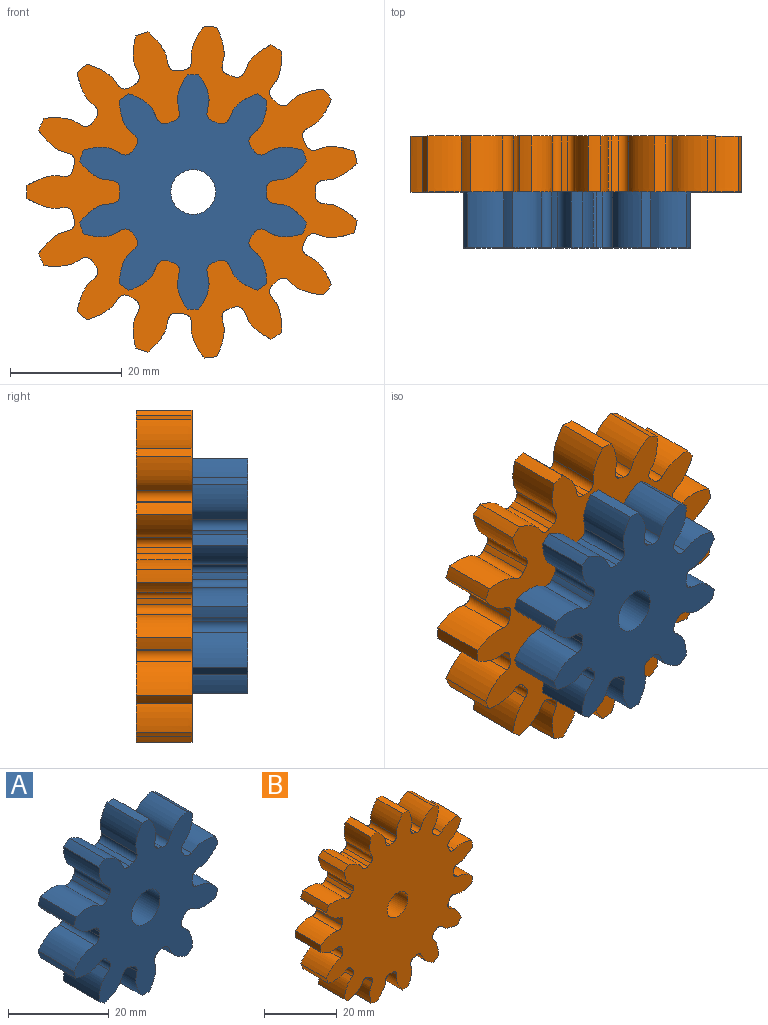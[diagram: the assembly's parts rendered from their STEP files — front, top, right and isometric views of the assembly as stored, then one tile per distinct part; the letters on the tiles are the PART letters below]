
ASSEMBLY  parts=2 mates=1
PART A: 63 faces, bbox 40.6x10x42.1 mm
  f0: cylinder r=21mm len=10mm, axis (0,1,0), area 20.5mm2, adj f9,f12,f53,f60
  f1: cylinder r=21mm len=10mm, axis (0,1,0), area 20.5mm2, adj f9,f12,f13,f55
  f2: cylinder r=21mm len=10mm, axis (0,1,0), area 20.5mm2, adj f9,f12,f43,f50
  f3: cylinder r=21mm len=10mm, axis (0,1,0), area 20.5mm2, adj f9,f12,f45,f58
  f4: cylinder r=21mm len=10mm, axis (0,1,0), area 20.5mm2, adj f9,f12,f33,f40
  f5: cylinder r=21mm len=10mm, axis (0,1,0), area 20.5mm2, adj f9,f12,f28,f35
  f6: cylinder r=21mm len=10mm, axis (0,1,0), area 20.5mm2, adj f9,f12,f23,f30
  f7: cylinder r=21mm len=10mm, axis (0,1,0), area 20.5mm2, adj f9,f12,f25,f48
  f8: cylinder r=21mm len=10mm, axis (0,1,0), area 20.5mm2, adj f9,f12,f20,f38
  f9: plane 42.07x40.62mm, normal (0,-1,0), area 870mm2, adj f0,f1,f2,f3,f4,f5,f6,f7
  f10: cylinder r=4mm len=10mm, axis (0,1,0), area 251.3mm2, adj f9,f12
  f11: cylinder r=21mm len=10mm, axis (0,1,0), area 20.5mm2, adj f9,f12,f15,f18
  f12: plane 42.07x40.62mm, normal (0,1,0), area 870mm2, adj f0,f1,f2,f3,f4,f5,f6,f7
  f13: extruded ~10x5.91mm, area 71mm2, adj f1,f9,f12,f16
  f14: cylinder r=13.12mm len=10mm, axis (0,1,0), area 11.2mm2, adj f9,f12,f16,f17
  f15: extruded ~10x5.91mm, area 71mm2, adj f9,f11,f12,f17
  f16: cylinder r=1.44mm len=10mm, axis (0,1,0), area 21.2mm2, adj f9,f12,f13,f14
  f17: cylinder r=1.44mm len=10mm, axis (0,1,0), area 21.2mm2, adj f9,f12,f14,f15
  f18: extruded ~10x6.81mm, area 71mm2, adj f9,f11,f12,f21
  f19: cylinder r=13.12mm len=10mm, axis (0,1,0), area 11.2mm2, adj f9,f12,f21,f22
  f20: extruded ~10x6.27mm, area 71mm2, adj f8,f9,f12,f22
  f21: cylinder r=1.44mm len=10mm, axis (0,1,0), area 21.2mm2, adj f9,f12,f18,f19
  f22: cylinder r=1.44mm len=10mm, axis (0,1,0), area 21.2mm2, adj f9,f12,f19,f20
  f23: extruded ~10x5.91mm, area 71mm2, adj f6,f9,f12,f26
  f24: cylinder r=13.12mm len=10mm, axis (0,1,0), area 11.2mm2, adj f9,f12,f26,f27
  f25: extruded ~10x5.91mm, area 71mm2, adj f7,f9,f12,f27
  f26: cylinder r=1.44mm len=10mm, axis (0,1,0), area 21.2mm2, adj f9,f12,f23,f24
  f27: cylinder r=1.44mm len=10mm, axis (0,1,0), area 21.2mm2, adj f9,f12,f24,f25
  f28: extruded ~10x6.27mm, area 71mm2, adj f5,f9,f12,f31
  f29: cylinder r=13.12mm len=10mm, axis (0,1,0), area 11.2mm2, adj f9,f12,f31,f32
  f30: extruded ~10x6.81mm, area 71mm2, adj f6,f9,f12,f32
  f31: cylinder r=1.44mm len=10mm, axis (0,1,0), area 21.2mm2, adj f9,f12,f28,f29
  f32: cylinder r=1.44mm len=10mm, axis (0,1,0), area 21.2mm2, adj f9,f12,f29,f30
  f33: extruded ~10x6.69mm, area 71mm2, adj f4,f9,f12,f36
  f34: cylinder r=13.12mm len=10mm, axis (0,1,0), area 11.2mm2, adj f9,f12,f36,f37
  f35: extruded ~10x5.11mm, area 71mm2, adj f5,f9,f12,f37
  f36: cylinder r=1.44mm len=10mm, axis (0,1,0), area 21.2mm2, adj f9,f12,f33,f34
  f37: cylinder r=1.44mm len=10mm, axis (0,1,0), area 21.2mm2, adj f9,f12,f34,f35
  f38: extruded ~10x5.11mm, area 71mm2, adj f8,f9,f12,f41
  f39: cylinder r=13.12mm len=10mm, axis (0,1,0), area 11.2mm2, adj f9,f12,f41,f42
  f40: extruded ~10x6.69mm, area 71mm2, adj f4,f9,f12,f42
  f41: cylinder r=1.44mm len=10mm, axis (0,1,0), area 21.2mm2, adj f9,f12,f38,f39
  f42: cylinder r=1.44mm len=10mm, axis (0,1,0), area 21.2mm2, adj f9,f12,f39,f40
  f43: extruded ~10x5.11mm, area 71mm2, adj f2,f9,f12,f46
  f44: cylinder r=13.12mm len=10mm, axis (0,1,0), area 11.2mm2, adj f9,f12,f46,f47
  f45: extruded ~10x6.69mm, area 71mm2, adj f3,f9,f12,f47
  f46: cylinder r=1.44mm len=10mm, axis (0,1,0), area 21.2mm2, adj f9,f12,f43,f44
  f47: cylinder r=1.44mm len=10mm, axis (0,1,0), area 21.2mm2, adj f9,f12,f44,f45
  f48: extruded ~10x6.81mm, area 71mm2, adj f7,f9,f12,f51
  f49: cylinder r=13.12mm len=10mm, axis (0,1,0), area 11.2mm2, adj f9,f12,f51,f52
  f50: extruded ~10x6.27mm, area 71mm2, adj f2,f9,f12,f52
  f51: cylinder r=1.44mm len=10mm, axis (0,1,0), area 21.2mm2, adj f9,f12,f48,f49
  f52: cylinder r=1.44mm len=10mm, axis (0,1,0), area 21.2mm2, adj f9,f12,f49,f50
  f53: extruded ~10x6.27mm, area 71mm2, adj f0,f9,f12,f56
  f54: cylinder r=13.12mm len=10mm, axis (0,1,0), area 11.2mm2, adj f9,f12,f56,f57
  f55: extruded ~10x6.81mm, area 71mm2, adj f1,f9,f12,f57
  f56: cylinder r=1.44mm len=10mm, axis (0,1,0), area 21.2mm2, adj f9,f12,f53,f54
  f57: cylinder r=1.44mm len=10mm, axis (0,1,0), area 21.2mm2, adj f9,f12,f54,f55
  f58: extruded ~10x6.69mm, area 71mm2, adj f3,f9,f12,f61
  f59: cylinder r=13.12mm len=10mm, axis (0,1,0), area 11.2mm2, adj f9,f12,f61,f62
  f60: extruded ~10x5.11mm, area 71mm2, adj f0,f9,f12,f62
  f61: cylinder r=1.44mm len=10mm, axis (0,1,0), area 21.2mm2, adj f9,f12,f58,f59
  f62: cylinder r=1.44mm len=10mm, axis (0,1,0), area 21.2mm2, adj f9,f12,f59,f60
PART B: 93 faces, bbox 59.1x10x59.5 mm
  f0: cylinder r=29.75mm len=10mm, axis (0,1,0), area 22.9mm2, adj f14,f17,f83,f90
  f1: cylinder r=29.75mm len=10mm, axis (0,1,0), area 22.9mm2, adj f14,f17,f73,f85
  f2: cylinder r=29.75mm len=10mm, axis (0,1,0), area 22.9mm2, adj f14,f17,f18,f80
  f3: cylinder r=29.75mm len=10mm, axis (0,1,0), area 22.9mm2, adj f14,f17,f75,f78
  f4: cylinder r=29.75mm len=10mm, axis (0,1,0), area 22.9mm2, adj f14,f17,f63,f70
  f5: cylinder r=29.75mm len=10mm, axis (0,1,0), area 22.9mm2, adj f14,f17,f65,f88
  f6: cylinder r=29.75mm len=10mm, axis (0,1,0), area 22.9mm2, adj f14,f17,f60,f68
  f7: cylinder r=29.75mm len=10mm, axis (0,1,0), area 22.9mm2, adj f14,f17,f55,f58
  f8: cylinder r=29.75mm len=10mm, axis (0,1,0), area 22.9mm2, adj f14,f17,f38,f50
  f9: cylinder r=29.75mm len=10mm, axis (0,1,0), area 22.9mm2, adj f14,f17,f45,f48
  f10: cylinder r=29.75mm len=10mm, axis (0,1,0), area 22.9mm2, adj f14,f17,f33,f40
  f11: cylinder r=29.75mm len=10mm, axis (0,1,0), area 22.9mm2, adj f14,f17,f23,f35
  f12: cylinder r=29.75mm len=10mm, axis (0,1,0), area 22.9mm2, adj f14,f17,f30,f53
  f13: cylinder r=29.75mm len=10mm, axis (0,1,0), area 22.9mm2, adj f14,f17,f25,f28
  f14: plane 59.46x59.13mm, normal (0,-1,0), area 2051.8mm2, adj f0,f1,f2,f3,f4,f5,f6,f7
  f15: cylinder r=4mm len=10mm, axis (0,1,0), area 251.3mm2, adj f14,f17
  f16: cylinder r=29.75mm len=10mm, axis (0,1,0), area 22.9mm2, adj f14,f17,f20,f43
  f17: plane 59.46x59.13mm, normal (0,1,0), area 2051.8mm2, adj f0,f1,f2,f3,f4,f5,f6,f7
  f18: extruded ~10x6.14mm, area 70.2mm2, adj f2,f14,f17,f21
  f19: cylinder r=21.88mm len=10mm, axis (0,1,0), area 12.3mm2, adj f14,f17,f21,f22
  f20: extruded ~10x6.14mm, area 70.2mm2, adj f14,f16,f17,f22
  f21: cylinder r=1.43mm len=10mm, axis (0,1,0), area 21.7mm2, adj f14,f17,f18,f19
  f22: cylinder r=1.43mm len=10mm, axis (0,1,0), area 21.7mm2, adj f14,f17,f19,f20
  f23: extruded ~10x6.81mm, area 70.2mm2, adj f11,f14,f17,f26
  f24: cylinder r=21.88mm len=10mm, axis (0,1,0), area 12.3mm2, adj f14,f17,f26,f27
  f25: extruded ~10x5.65mm, area 70.2mm2, adj f13,f14,f17,f27
  f26: cylinder r=1.43mm len=10mm, axis (0,1,0), area 21.7mm2, adj f14,f17,f23,f24
  f27: cylinder r=1.43mm len=10mm, axis (0,1,0), area 21.7mm2, adj f14,f17,f24,f25
  f28: extruded ~10x6.02mm, area 70.2mm2, adj f13,f14,f17,f31
  f29: cylinder r=21.88mm len=10mm, axis (0,1,0), area 12.3mm2, adj f14,f17,f31,f32
  f30: extruded ~10x6.72mm, area 70.2mm2, adj f12,f14,f17,f32
  f31: cylinder r=1.43mm len=10mm, axis (0,1,0), area 21.7mm2, adj f14,f17,f28,f29
  f32: cylinder r=1.43mm len=10mm, axis (0,1,0), area 21.7mm2, adj f14,f17,f29,f30
  f33: extruded ~10x6.42mm, area 70.2mm2, adj f10,f14,f17,f36
  f34: cylinder r=21.88mm len=10mm, axis (0,1,0), area 12.3mm2, adj f14,f17,f36,f37
  f35: extruded ~10x5.8mm, area 70.2mm2, adj f11,f14,f17,f37
  f36: cylinder r=1.43mm len=10mm, axis (0,1,0), area 21.7mm2, adj f14,f17,f33,f34
  f37: cylinder r=1.43mm len=10mm, axis (0,1,0), area 21.7mm2, adj f14,f17,f34,f35
  f38: extruded ~10x4.92mm, area 70.2mm2, adj f8,f14,f17,f41
  f39: cylinder r=21.88mm len=10mm, axis (0,1,0), area 12.3mm2, adj f14,f17,f41,f42
  f40: extruded ~10x6.76mm, area 70.2mm2, adj f10,f14,f17,f42
  f41: cylinder r=1.43mm len=10mm, axis (0,1,0), area 21.7mm2, adj f14,f17,f38,f39
  f42: cylinder r=1.43mm len=10mm, axis (0,1,0), area 21.7mm2, adj f14,f17,f39,f40
  f43: extruded ~10x6.82mm, area 70.2mm2, adj f14,f16,f17,f46
  f44: cylinder r=21.88mm len=10mm, axis (0,1,0), area 12.3mm2, adj f14,f17,f46,f47
  f45: extruded ~10x5.22mm, area 70.2mm2, adj f9,f14,f17,f47
  f46: cylinder r=1.43mm len=10mm, axis (0,1,0), area 21.7mm2, adj f14,f17,f43,f44
  f47: cylinder r=1.43mm len=10mm, axis (0,1,0), area 21.7mm2, adj f14,f17,f44,f45
  f48: extruded ~10x6.32mm, area 70.2mm2, adj f9,f14,f17,f51
  f49: cylinder r=21.88mm len=10mm, axis (0,1,0), area 12.3mm2, adj f14,f17,f51,f52
  f50: extruded ~10x6.56mm, area 70.2mm2, adj f8,f14,f17,f52
  f51: cylinder r=1.43mm len=10mm, axis (0,1,0), area 21.7mm2, adj f14,f17,f48,f49
  f52: cylinder r=1.43mm len=10mm, axis (0,1,0), area 21.7mm2, adj f14,f17,f49,f50
  f53: extruded ~10x5.39mm, area 70.2mm2, adj f12,f14,f17,f56
  f54: cylinder r=21.88mm len=10mm, axis (0,1,0), area 12.3mm2, adj f14,f17,f56,f57
  f55: extruded ~10x6.63mm, area 70.2mm2, adj f7,f14,f17,f57
  f56: cylinder r=1.43mm len=10mm, axis (0,1,0), area 21.7mm2, adj f14,f17,f53,f54
  f57: cylinder r=1.43mm len=10mm, axis (0,1,0), area 21.7mm2, adj f14,f17,f54,f55
  f58: extruded ~10x6.63mm, area 70.2mm2, adj f7,f14,f17,f61
  f59: cylinder r=21.88mm len=10mm, axis (0,1,0), area 12.3mm2, adj f14,f17,f61,f62
  f60: extruded ~10x5.39mm, area 70.2mm2, adj f6,f14,f17,f62
  f61: cylinder r=1.43mm len=10mm, axis (0,1,0), area 21.7mm2, adj f14,f17,f58,f59
  f62: cylinder r=1.43mm len=10mm, axis (0,1,0), area 21.7mm2, adj f14,f17,f59,f60
  f63: extruded ~10x5.65mm, area 70.2mm2, adj f4,f14,f17,f66
  f64: cylinder r=21.88mm len=10mm, axis (0,1,0), area 12.3mm2, adj f14,f17,f66,f67
  f65: extruded ~10x6.81mm, area 70.2mm2, adj f5,f14,f17,f67
  f66: cylinder r=1.43mm len=10mm, axis (0,1,0), area 21.7mm2, adj f14,f17,f63,f64
  f67: cylinder r=1.43mm len=10mm, axis (0,1,0), area 21.7mm2, adj f14,f17,f64,f65
  f68: extruded ~10x6.72mm, area 70.2mm2, adj f6,f14,f17,f71
  f69: cylinder r=21.88mm len=10mm, axis (0,1,0), area 12.3mm2, adj f14,f17,f71,f72
  f70: extruded ~10x6.02mm, area 70.2mm2, adj f4,f14,f17,f72
  f71: cylinder r=1.43mm len=10mm, axis (0,1,0), area 21.7mm2, adj f14,f17,f68,f69
  f72: cylinder r=1.43mm len=10mm, axis (0,1,0), area 21.7mm2, adj f14,f17,f69,f70
  f73: extruded ~10x6.56mm, area 70.2mm2, adj f1,f14,f17,f76
  f74: cylinder r=21.88mm len=10mm, axis (0,1,0), area 12.3mm2, adj f14,f17,f76,f77
  f75: extruded ~10x6.32mm, area 70.2mm2, adj f3,f14,f17,f77
  f76: cylinder r=1.43mm len=10mm, axis (0,1,0), area 21.7mm2, adj f14,f17,f73,f74
  f77: cylinder r=1.43mm len=10mm, axis (0,1,0), area 21.7mm2, adj f14,f17,f74,f75
  f78: extruded ~10x5.22mm, area 70.2mm2, adj f3,f14,f17,f81
  f79: cylinder r=21.88mm len=10mm, axis (0,1,0), area 12.3mm2, adj f14,f17,f81,f82
  f80: extruded ~10x6.82mm, area 70.2mm2, adj f2,f14,f17,f82
  f81: cylinder r=1.43mm len=10mm, axis (0,1,0), area 21.7mm2, adj f14,f17,f78,f79
  f82: cylinder r=1.43mm len=10mm, axis (0,1,0), area 21.7mm2, adj f14,f17,f79,f80
  f83: extruded ~10x6.76mm, area 70.2mm2, adj f0,f14,f17,f86
  f84: cylinder r=21.88mm len=10mm, axis (0,1,0), area 12.3mm2, adj f14,f17,f86,f87
  f85: extruded ~10x4.92mm, area 70.2mm2, adj f1,f14,f17,f87
  f86: cylinder r=1.43mm len=10mm, axis (0,1,0), area 21.7mm2, adj f14,f17,f83,f84
  f87: cylinder r=1.43mm len=10mm, axis (0,1,0), area 21.7mm2, adj f14,f17,f84,f85
  f88: extruded ~10x5.8mm, area 70.2mm2, adj f5,f14,f17,f91
  f89: cylinder r=21.88mm len=10mm, axis (0,1,0), area 12.3mm2, adj f14,f17,f91,f92
  f90: extruded ~10x6.42mm, area 70.2mm2, adj f0,f14,f17,f92
  f91: cylinder r=1.43mm len=10mm, axis (0,1,0), area 21.7mm2, adj f14,f17,f88,f89
  f92: cylinder r=1.43mm len=10mm, axis (0,1,0), area 21.7mm2, adj f14,f17,f89,f90
PLACE A t=(0,-10,0)mm
PLACE B at identity
MATE fastened B.f0 <-> A.f0  axis (0,-1,0) through (0,-10,0)mm
